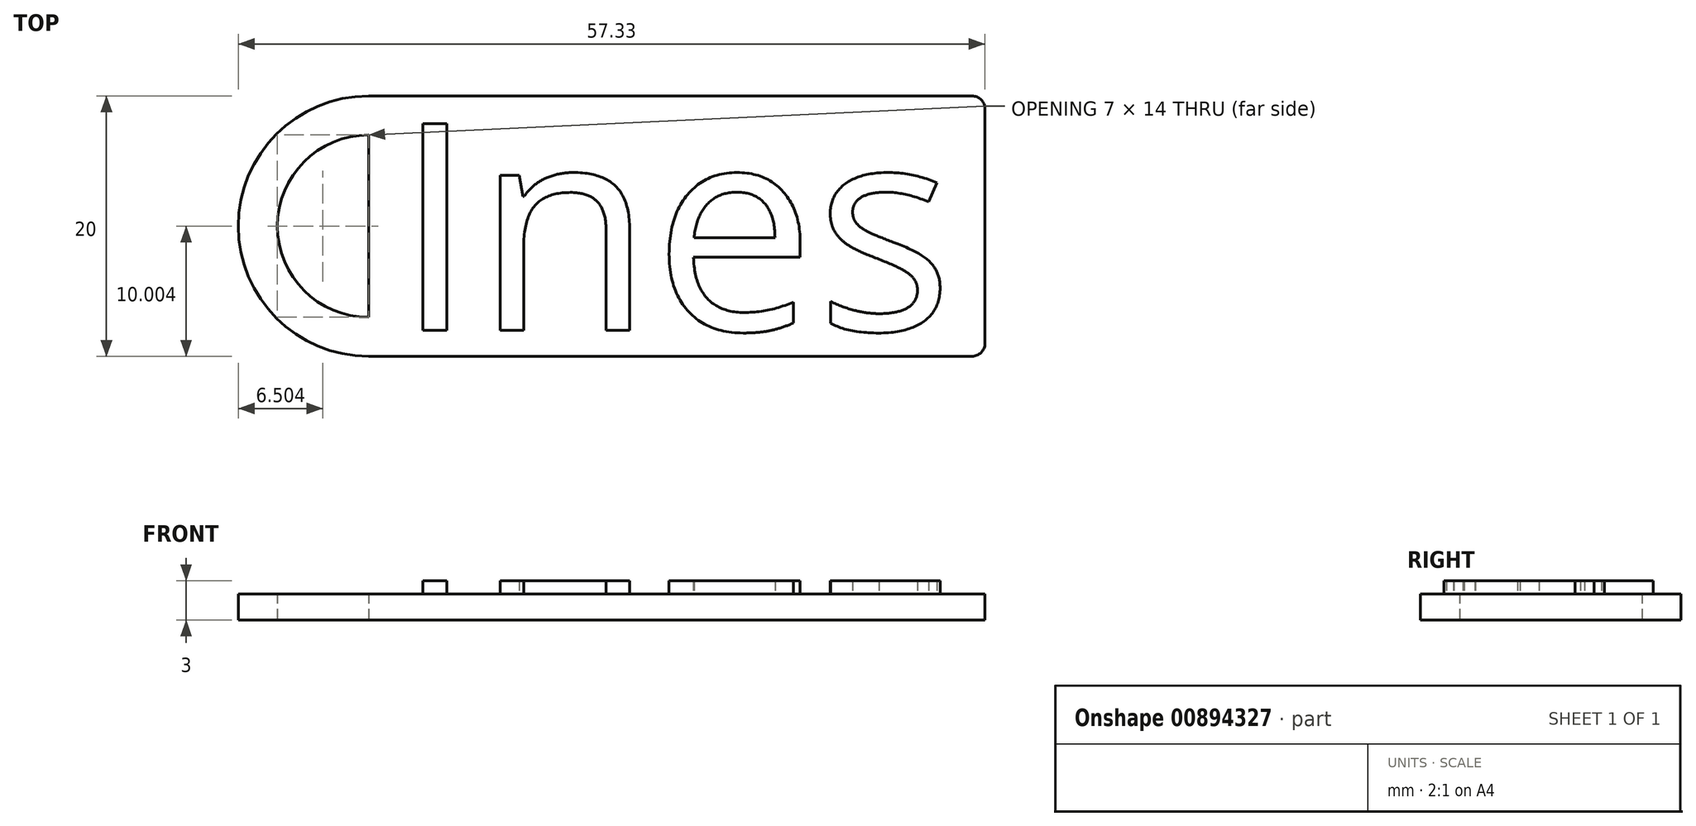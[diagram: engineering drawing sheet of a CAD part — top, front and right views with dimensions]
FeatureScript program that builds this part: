
annotation { "Feature Type Name" : "Feature", "Feature Type Description" : "" }
export const myFeature = defineFeature(function(context is Context, id is Id, definition is map)
    precondition{}
    {
        {
            var Q0;
            Q0=qCreatedBy(makeId("Top.planeOp"),FACE);
            var sketch = newSketch(context, id + "F0", { "sketchPlane" : qUnion([Q0])});
            skText(sketch, "E0", { "text": "Ines", "fontName": "OpenSans-Regular.ttf"});
            skLineSegment(sketch, "E1.bottom", {"start": v(-18.55, 9.8) * mm, "end": v(28.78, 9.8) * mm});
            skLineSegment(sketch, "E1.top", {"start": v(-18.55, -10.2) * mm, "end": v(28.78, -10.2) * mm});
            skLineSegment(sketch, "E1.left", {"start": v(-18.55, 9.8) * mm, "end": v(-18.55, -10.2) * mm});
            skLineSegment(sketch, "E1.right", {"start": v(28.78, 9.8) * mm, "end": v(28.78, -10.2) * mm});
            skPoint(sketch, "E2.third.point", {"position": v(-26.99, -2.08) * mm});
            skArc(sketch, "E3", {"start": v(-18.55, 9.8) * mm, "mid": v(-28.55, -0.2) * mm, "end": v(-18.55, -10.2) * mm});
            skArc(sketch, "E4", {"start": v(-18.55, 6.8) * mm, "mid": v(-25.55, -0.2) * mm, "end": v(-18.55, -7.2) * mm});
            const initialGuessF0  = {"E0": [-0.01655, -0.0082, 1, 0, 0.016]};
            skSetInitialGuess(sketch, initialGuessF0);
            skSolve(sketch);
        }
        {
            var Q0;
            {var subQ0=sQuery(id+"F0.wireOp",EDGE,"E3");Q0=makeQuery(id+"F0.imprint","IMPRINT",FACE,{"disambiguationData":[TD([[makeQuery(id+"F0.imprint","IMPRINT",EDGE,{"derivedFrom":subQ0}),1.0]])]});}
            var Q1;
            Q1 = qSketchRegion(id + "F0", true);
            var Q2;
            Q2=makeQuery(id+"F0.imprint","IMPRINT",FACE,{"disambiguationData":[TD([[makeQuery(id+"F0.imprint","IMPRINT",EDGE,{"derivedFrom":sQuery(id+"F0.wireOp",EDGE,"E0.sketch_text.stroke-0")}),-1.0]])]});
            var Q3;
            Q3=makeQuery(id+"F0.imprint","IMPRINT",FACE,{"disambiguationData":[TD([[makeQuery(id+"F0.imprint","IMPRINT",EDGE,{"derivedFrom":sQuery(id+"F0.wireOp",EDGE,"E0.sketch_text.stroke-40")}),-1.0]])]});
            var Q4;
            Q4=makeQuery(id+"F0.imprint","IMPRINT",FACE,{"disambiguationData":[TD([[makeQuery(id+"F0.imprint","IMPRINT",EDGE,{"derivedFrom":sQuery(id+"F0.wireOp",EDGE,"E0.sketch_text.stroke-21")}),-1.0]])]});
            var Q5;
            Q5=makeQuery(id+"F0.imprint","IMPRINT",FACE,{"disambiguationData":[TD([[makeQuery(id+"F0.imprint","IMPRINT",EDGE,{"derivedFrom":sQuery(id+"F0.wireOp",EDGE,"E0.sketch_text.stroke-4")}),-1.0]])]});
            var Q6;
            Q6=makeQuery(id+"F0.imprint","IMPRINT",FACE,{"disambiguationData":[TD([[makeQuery(id+"F0.imprint","IMPRINT",EDGE,{"derivedFrom":sQuery(id+"F0.wireOp",EDGE,"E0.sketch_text.stroke-0")}),1.0]])]});
            var Q7;
            Q7=makeQuery(id+"F0.imprint","IMPRINT",FACE,{"disambiguationData":[TD([[makeQuery(id+"F0.imprint","IMPRINT",EDGE,{"derivedFrom":sQuery(id+"F0.wireOp",EDGE,"E0.sketch_text.stroke-35")}),1.0]])]});
            extrude(context, id + "F1", {"entities" : qUnion([Q0, Q1, Q2, Q3, Q4, Q5, Q6, Q7]), "depth" : 2 * mm, "offsetDistance" : 25 * mm});
        }
        {
            var Q0;
            Q0=makeQuery(id+"F0.imprint","IMPRINT",FACE,{"disambiguationData":[TD([[makeQuery(id+"F0.imprint","IMPRINT",EDGE,{"derivedFrom":sQuery(id+"F0.wireOp",EDGE,"E0.sketch_text.stroke-0")}),-1.0]])]});
            var Q1;
            Q1=makeQuery(id+"F0.imprint","IMPRINT",FACE,{"disambiguationData":[TD([[makeQuery(id+"F0.imprint","IMPRINT",EDGE,{"derivedFrom":sQuery(id+"F0.wireOp",EDGE,"E0.sketch_text.stroke-4")}),-1.0]])]});
            var Q2;
            Q2=makeQuery(id+"F0.imprint","IMPRINT",FACE,{"disambiguationData":[TD([[makeQuery(id+"F0.imprint","IMPRINT",EDGE,{"derivedFrom":sQuery(id+"F0.wireOp",EDGE,"E0.sketch_text.stroke-21")}),-1.0]])]});
            var Q3;
            Q3=makeQuery(id+"F0.imprint","IMPRINT",FACE,{"disambiguationData":[TD([[makeQuery(id+"F0.imprint","IMPRINT",EDGE,{"derivedFrom":sQuery(id+"F0.wireOp",EDGE,"E0.sketch_text.stroke-40")}),-1.0]])]});
            extrude(context, id + "F2", {"entities" : qUnion([Q0, Q1, Q2, Q3]), "operationType" : NewBodyOperationType.ADD, "depth" : 3 * mm, "offsetDistance" : 25 * mm});
        }
        {
            var Q0;
            Q0=makeQuery(id+"F1.opExtrude","SWEPT_EDGE",EDGE,{"disambiguationData":[OSD([sQuery(id+"F0.wireOp",EDGE,"E1.bottom"),sQuery(id+"F0.wireOp",EDGE,"E1.right")])]});
            var Q1;
            Q1=makeQuery(id+"F1.opExtrude","SWEPT_EDGE",EDGE,{"disambiguationData":[OSD([sQuery(id+"F0.wireOp",EDGE,"E1.top"),sQuery(id+"F0.wireOp",EDGE,"E1.right")])]});
            fillet(context, id + "F3", {"entities" : qUnion([Q0, Q1]), "radius" : 1 * mm, "tangentPropagation" : true, "allowEdgeOverflow" : false});
        }
    });
